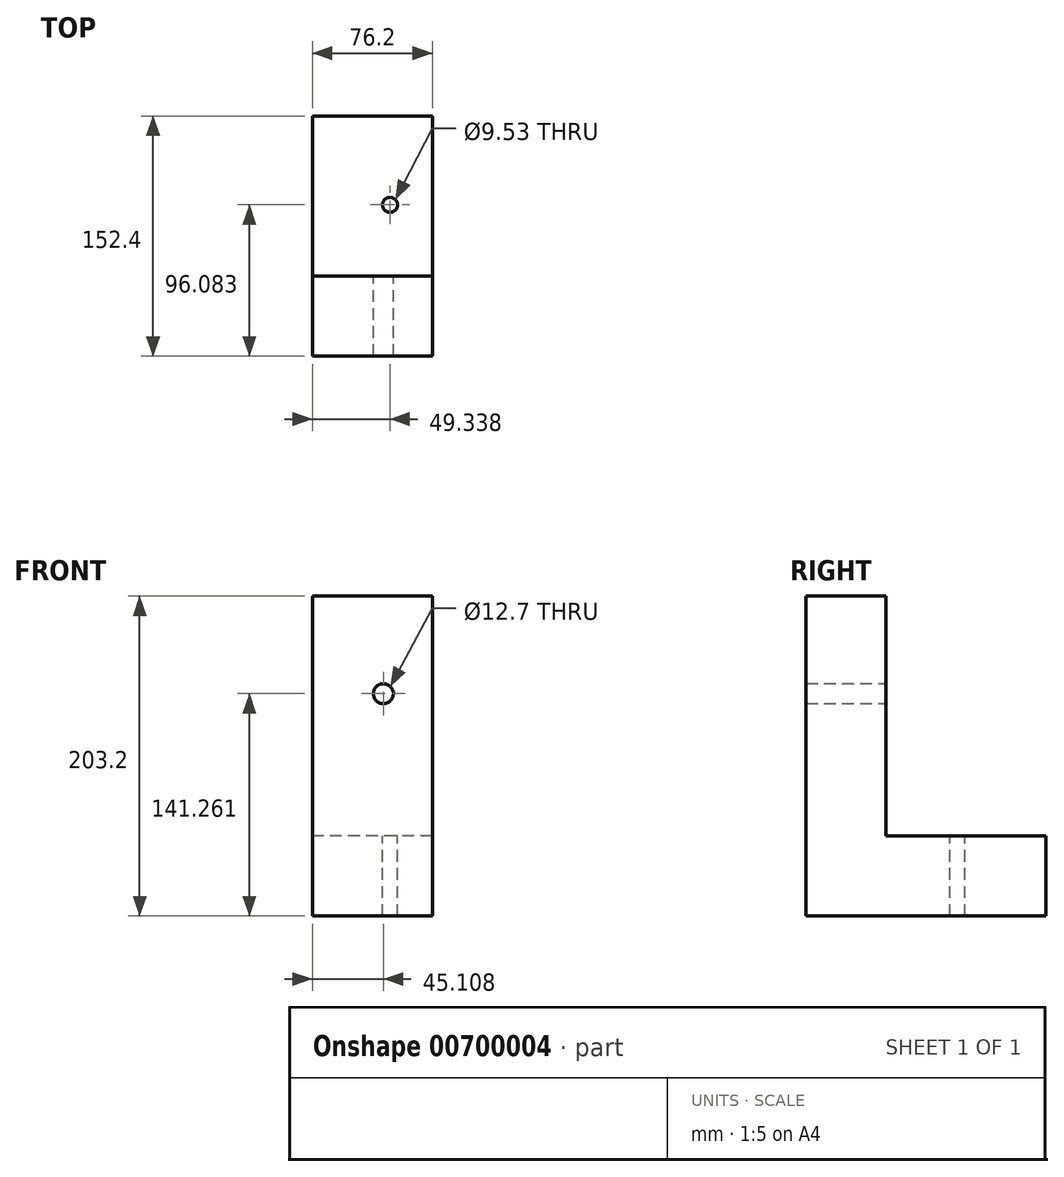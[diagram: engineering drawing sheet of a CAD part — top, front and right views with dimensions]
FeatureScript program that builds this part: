
annotation { "Feature Type Name" : "Feature", "Feature Type Description" : "" }
export const myFeature = defineFeature(function(context is Context, id is Id, definition is map)
    precondition{}
    {
        {
            var Q0;
            Q0=qCreatedBy(makeId("Right.planeOp"),FACE);
            var sketch = newSketch(context, id + "F0", { "sketchPlane" : qUnion([Q0])});
            skLineSegment(sketch, "E0", {"start": v(-152.4, 0) * mm, "end": v(-152.4, 203.2) * mm});
            skLineSegment(sketch, "E1", {"start": v(-152.4, 203.2) * mm, "end": v(-101.6, 203.2) * mm});
            skLineSegment(sketch, "E2", {"start": v(-101.6, 203.2) * mm, "end": v(-101.6, 50.8) * mm});
            skLineSegment(sketch, "E3", {"start": v(-152.4, 0) * mm, "end": v(0, 0) * mm});
            skLineSegment(sketch, "E4", {"start": v(-101.6, 50.8) * mm, "end": v(0, 50.8) * mm});
            skLineSegment(sketch, "E5", {"start": v(0, 50.8) * mm, "end": v(0, 0) * mm});
            skSolve(sketch);
        }
        {
            var Q0;
            Q0=makeQuery(id+"F0.imprint","IMPRINT",FACE,{"disambiguationData":[TD([[makeQuery(id+"F0.imprint","IMPRINT",EDGE,{"derivedFrom":sQuery(id+"F0.wireOp",EDGE,"E0")}),-1.0]])]});
            extrude(context, id + "F1", {"entities" : qUnion([Q0]), "depth" : 76.2 * mm, "offsetDistance" : 25.4 * mm});
        }
        {
            var Q0;
            Q0=makeQuery(id+"F1.opExtrude","SWEPT_FACE",FACE,{"disambiguationData":[OSD([sQuery(id+"F0.wireOp",EDGE,"E4")])]});
            var sketch = newSketch(context, id + "F2", { "sketchPlane" : qUnion([Q0])});
            skCircle(sketch, "E6", {"center": v(49.34, -56.32) * mm, "radius": 4.5 * mm});
            skSolve(sketch);
        }
        {
            var Q0;
            Q0=sQuery(id+"F2.wireOp",VERTEX,"E6.center");
            var Q1;
            Q1=makeQuery(id+"F1.opExtrude","SWEPT_BODY",BODY,{"disambiguationData":[OSD([sQuery(id+"F0.wireOp",EDGE,"E0"),sQuery(id+"F0.wireOp",EDGE,"E1"),sQuery(id+"F0.wireOp",EDGE,"E2"),sQuery(id+"F0.wireOp",EDGE,"E3"),sQuery(id+"F0.wireOp",EDGE,"E4"),sQuery(id+"F0.wireOp",EDGE,"E5")])]});
            hole(context, id + "F3", {"style" : HoleStyle.SIMPLE, "endStyle" : HoleEndStyle.THROUGH, "holeDiameter" : 9.52 * mm, "majorDiameter" : 6.35 * mm, "isTappedThrough" : true, "tappedDepth" : 12.7 * mm, "tapClearance" : 3, "locations" : qUnion([Q0]), "scope" : qUnion([Q1])});
        }
        {
            var Q0;
            Q0=makeQuery(id+"F1.opExtrude","SWEPT_FACE",FACE,{"disambiguationData":[OSD([sQuery(id+"F0.wireOp",EDGE,"E2")])]});
            var sketch = newSketch(context, id + "F4", { "sketchPlane" : qUnion([Q0])});
            skCircle(sketch, "E7", {"center": v(-45.1, 141.26) * mm, "radius": 6.35 * mm});
            skSolve(sketch);
        }
        {
            var Q0;
            Q0=sQuery(id+"F4.wireOp",VERTEX,"E7.center");
            var Q1;
            Q1=makeQuery(id+"F1.opExtrude","SWEPT_BODY",BODY,{"disambiguationData":[OSD([sQuery(id+"F0.wireOp",EDGE,"E0"),sQuery(id+"F0.wireOp",EDGE,"E1"),sQuery(id+"F0.wireOp",EDGE,"E2"),sQuery(id+"F0.wireOp",EDGE,"E3"),sQuery(id+"F0.wireOp",EDGE,"E4"),sQuery(id+"F0.wireOp",EDGE,"E5")])]});
            hole(context, id + "F5", {"style" : HoleStyle.SIMPLE, "endStyle" : HoleEndStyle.THROUGH, "holeDiameter" : 12.7 * mm, "majorDiameter" : 6.35 * mm, "isTappedThrough" : true, "tappedDepth" : 12.7 * mm, "tapClearance" : 3, "locations" : qUnion([Q0]), "scope" : qUnion([Q1])});
        }
    });
